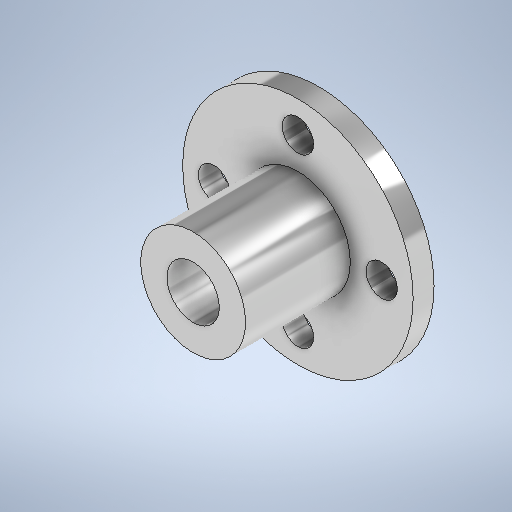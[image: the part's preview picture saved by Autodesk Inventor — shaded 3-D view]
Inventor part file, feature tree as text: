
AUTODESK INVENTOR PART (.ipt)
format: ipt  version: 2025 (Build 290162000, 162)  size: 261,120 bytes
history: native  units: mm
features: sketch x4, extrude x2, hole x2, other x1
ambient origin geometry x8: Origin, YZ Plane, XZ Plane, XY Plane, X Axis, Y Axis, Z Axis, Center Point
bodies: Body1 (feature_tree)
feature tree (9):
  other  "ソリッド1"
  extrude  "押し出し1"  Depth=22.0mm
  extrude  "押し出し2"  Depth=2.0mm TaperAngle=0.0deg
  hole  "穴1"  [1 undecoded]
  hole  "穴2"  [1 undecoded]
  sketch  "スケッチ1"
  sketch  "スケッチ2"
  sketch  "スケッチ3"
  sketch  "スケッチ4"
note: 2 required parameter values undecoded (feature->parameter linkage not recoverable at this tier; creation-order binding heuristic only, values carry confidence <= 0.55)
